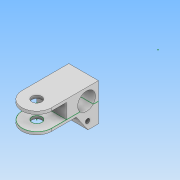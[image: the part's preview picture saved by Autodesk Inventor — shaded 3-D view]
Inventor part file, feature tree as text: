
AUTODESK INVENTOR PART (.ipt)
format: ipt  version: 2021 (Build 250183000, 183)  size: 142,336 bytes
history: native  units: mm
features: sketch x4, other x3, extrude x3, projected_geometry x3
ambient origin geometry x8: Origin, YZ Plane, XZ Plane, XY Plane, X Axis, Y Axis, Z Axis, Center Point
bodies: Body1 (feature_tree)
feature tree (13):
  other  "實體1"
  extrude  "擠出1"  Depth=250.0mm
  extrude  "擠出2"  Depth=100.0mm
  extrude  "擠出3"  Depth=208.571mm TaperAngle=0.0deg
  other  "螺紋1"
  sketch  "草圖4"
  sketch  "草圖1"
  sketch  "草圖2"
  projected_geometry  "投影迴路1"
  sketch  "草圖3"
  projected_geometry  "投影迴路2"
  projected_geometry  "投影迴路3"
  other  "投影切割邊1"
